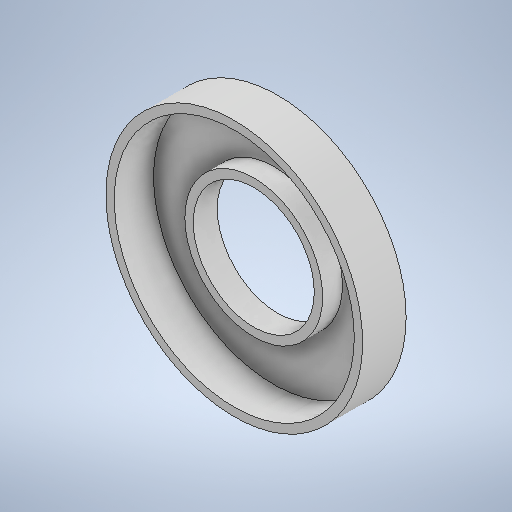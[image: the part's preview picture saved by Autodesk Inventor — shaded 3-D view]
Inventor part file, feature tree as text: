
AUTODESK INVENTOR PART (.ipt)
format: ipt  version: 2025.2 (Build 292293000, 293)  size: 268,288 bytes
history: native  units: in
note: dims shown in document units (in); Inventor stores cm internally (conversion verified against a paired STEP export)
features: extrude x4, sketch x4
ambient origin geometry x8: Origin, YZ Plane, XZ Plane, XY Plane, X Axis, Y Axis, Z Axis, Center Point
bodies: Solid1 (feature_tree)
feature tree (8):
  extrude  "Extrusion1"  Depth=0.0787in TaperAngle=0.0deg
  extrude  "Extrusion2"  Depth=0.7421in
  extrude  "Extrusion3"  Depth=0.1575in
  extrude  "Extrusion4"  Depth=0.374in
  sketch  "Sketch1"  dims[d0=4.8425in d1=0.0787in d2=0.0in]
  sketch  "Sketch2"  dims[d4=0.7421in d5=0.0in d6=2.2835in]
  sketch  "Sketch3"  dims[d7=0.0in d8=0.0in d9=0.1575in]
  sketch  "Sketch4"  dims[d10=0.374in d11=0.0in d12=4.5276in]
